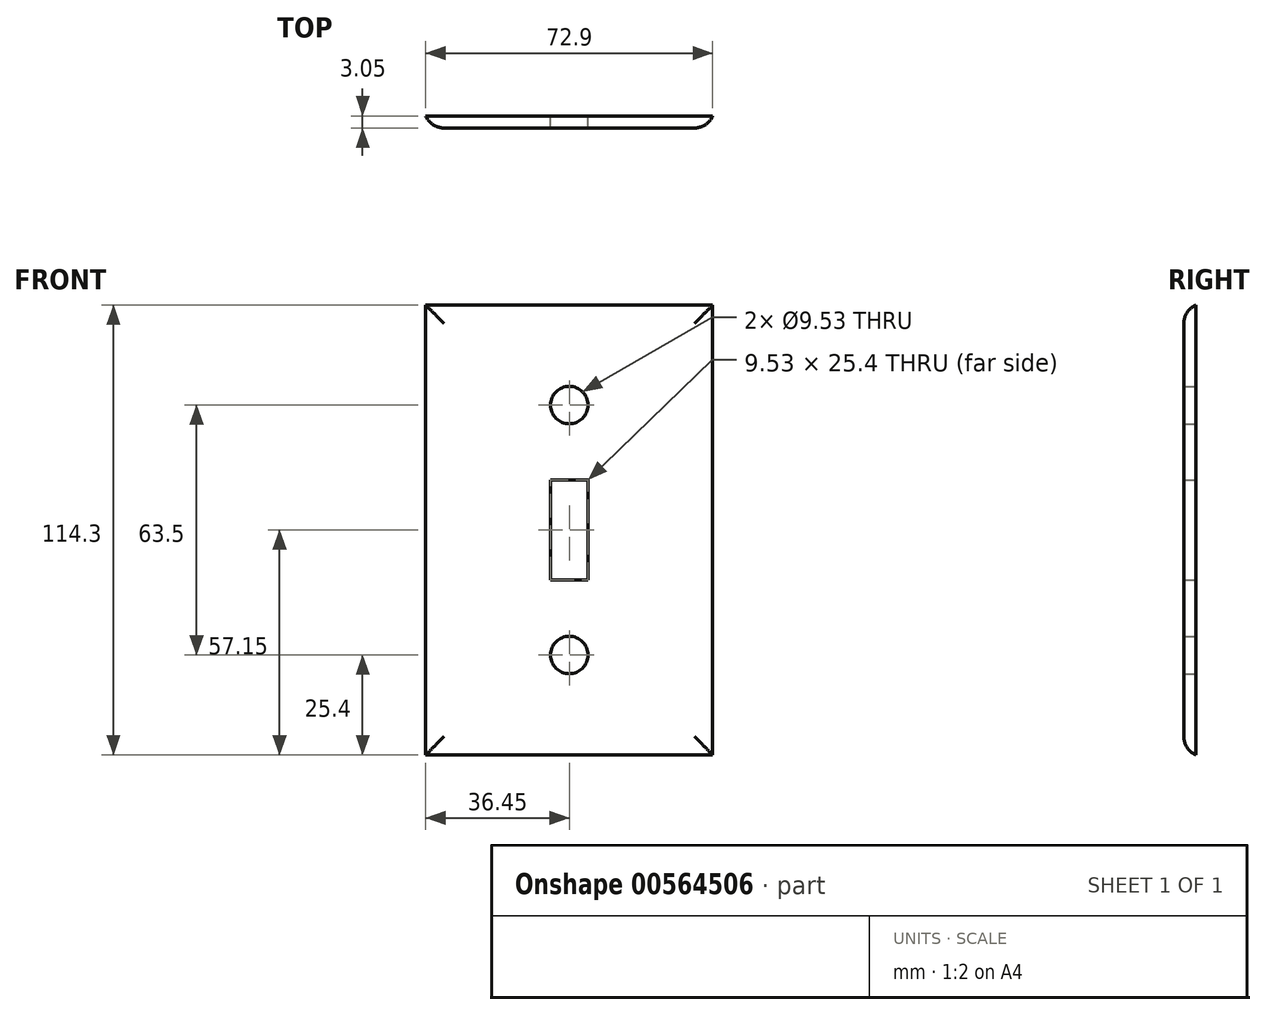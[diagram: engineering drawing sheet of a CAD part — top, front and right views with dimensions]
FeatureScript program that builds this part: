
annotation { "Feature Type Name" : "Feature", "Feature Type Description" : "" }
export const myFeature = defineFeature(function(context is Context, id is Id, definition is map)
    precondition{}
    {
        {
            var Q0;
            Q0=qCreatedBy(makeId("Front.planeOp"),FACE);
            var sketch = newSketch(context, id + "F0", { "sketchPlane" : qUnion([Q0])});
            skLineSegment(sketch, "E0.bottom", {"start": v(36.45, 57.15) * mm, "end": v(-36.45, 57.15) * mm});
            skLineSegment(sketch, "E0.top", {"start": v(36.45, -57.15) * mm, "end": v(-36.45, -57.15) * mm});
            skLineSegment(sketch, "E0.left", {"start": v(36.45, 57.15) * mm, "end": v(36.45, -57.15) * mm});
            skLineSegment(sketch, "E0.right", {"start": v(-36.45, 57.15) * mm, "end": v(-36.45, -57.15) * mm});
            skPoint(sketch, "E0.middle", {"position": v(0, 0) * mm});
            skLineSegment(sketch, "E1.bottom", {"start": v(-4.76, 12.7) * mm, "end": v(4.76, 12.7) * mm});
            skLineSegment(sketch, "E1.top", {"start": v(-4.76, -12.7) * mm, "end": v(4.76, -12.7) * mm});
            skLineSegment(sketch, "E1.left", {"start": v(-4.76, 12.7) * mm, "end": v(-4.76, -12.7) * mm});
            skLineSegment(sketch, "E1.right", {"start": v(4.76, 12.7) * mm, "end": v(4.76, -12.7) * mm});
            skCircle(sketch, "E2", {"center": v(0, -31.75) * mm, "radius": 4.76 * mm});
            skCircle(sketch, "E3", {"center": v(0, 31.75) * mm, "radius": 4.76 * mm});
            skSolve(sketch);
        }
        {
            var Q0;
            Q0=makeQuery(id+"F0.imprint","IMPRINT",FACE,{"disambiguationData":[TD([[makeQuery(id+"F0.imprint","IMPRINT",EDGE,{"derivedFrom":sQuery(id+"F0.wireOp",EDGE,"E0.bottom")}),1.0]])]});
            extrude(context, id + "F1", {"entities" : qUnion([Q0]), "depth" : 3.05 * mm, "offsetDistance" : 25.4 * mm});
        }
        {
            var Q0;
            Q0=makeQuery(id+"F1.opExtrude","CAP_EDGE",EDGE,{"disambiguationData":[OSD([sQuery(id+"F0.wireOp",EDGE,"E0.bottom")])],"isStart":false});
            var Q1;
            Q1=makeQuery(id+"F1.opExtrude","CAP_EDGE",EDGE,{"disambiguationData":[OSD([sQuery(id+"F0.wireOp",EDGE,"E0.left")])],"isStart":false});
            var Q2;
            Q2=makeQuery(id+"F1.opExtrude","CAP_EDGE",EDGE,{"disambiguationData":[OSD([sQuery(id+"F0.wireOp",EDGE,"E0.top")])],"isStart":false});
            var Q3;
            Q3=makeQuery(id+"F1.opExtrude","CAP_EDGE",EDGE,{"disambiguationData":[OSD([sQuery(id+"F0.wireOp",EDGE,"E0.right")])],"isStart":false});
            fillet(context, id + "F2", {"entities" : qUnion([Q0, Q1, Q2, Q3]), "radius" : 5.08 * mm, "tangentPropagation" : true, "allowEdgeOverflow" : false});
        }
    });
